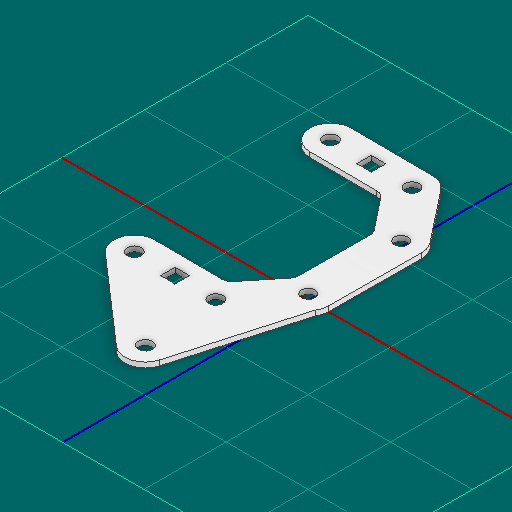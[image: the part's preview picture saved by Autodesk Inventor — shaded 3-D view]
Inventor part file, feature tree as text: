
AUTODESK INVENTOR PART (.ipt)
format: ipt  version: 2025 (Build 290162000, 162)  size: 179,200 bytes
history: native  units: in
note: dims shown in document units (in); Inventor stores cm internally (conversion verified against a paired STEP export)
features: other x8, extrude x1, sketch x1, reference x1
ambient origin geometry x8: Origin, YZ Plane, XZ Plane, XY Plane, X Axis, Y Axis, Z Axis, Center Point
bodies: Solid1 (feature_tree)
feature tree (11):
  other  "Blocks"
  extrude  "Extrusion1"  Depth=0.5in
  sketch  "Sketch1"  dims[d0=0.5in d1=0.5in d2=0.5in d3=0.125in d4=0.0625in d5=0.0in d6=0.176in d7=0.176in d8=0.176in d9=0.176in d10=0.5in d11=0.5in d12=0.25in d13=0.25in d14=0.625in d15=0.625in d16=0.5in d18=0.5in]
  other  "main_gusset"
  reference  "Reference2"
  other  "main_gusset:1"
  other  "<userpath>\vex_robotics_high_stakes\hardware\cad\ATLAS\chassis\drivetrain.iam"
  other  "drivetrain.iam"
  other  "!structure:1"
  other  "rail:1"
  other  "Alu Angle 1x1x12:1"
